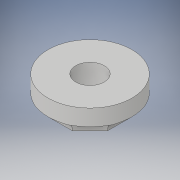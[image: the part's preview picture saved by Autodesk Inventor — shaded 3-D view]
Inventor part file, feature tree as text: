
AUTODESK INVENTOR PART (.ipt)
format: ipt  version: 2019 (Build 230136000, 136)  size: 127,488 bytes
history: native  units: mm
features: sketch x3, extrude x2, pattern_circular x1, hole x1
ambient origin geometry x8: Origin, YZ Plane, XZ Plane, XY Plane, X Axis, Y Axis, Z Axis, Center Point
bodies: Solid1 (feature_tree)
feature tree (7):
  extrude  "Extrusion1"  Depth=5.0mm TaperAngle=0.0deg
  extrude  "Extrusion2"  Depth=8.0mm TaperAngle=0.0deg
  pattern_circular  "Circular Pattern1"  Count=8 Angle=360.0deg
  hole  "Hole1"  [1 undecoded]
  sketch  "Sketch1"  dims[d0=15.0mm d1=5.0mm d2=0.0mm]
  sketch  "Sketch2"  dims[d3=4.2mm d4=8.0mm d5=0.0mm d6=80.0mm d7=360.0deg]
  sketch  "Sketch3"  dims[d9=5.1mm d10=3.8mm d11=6.0mm d12=5.1mm d13=3.8mm d14=90.0deg d15=8.0mm d16=20.594885mm]
note: 1 required parameter value undecoded (feature->parameter linkage not recoverable at this tier; creation-order binding heuristic only, values carry confidence <= 0.55)
